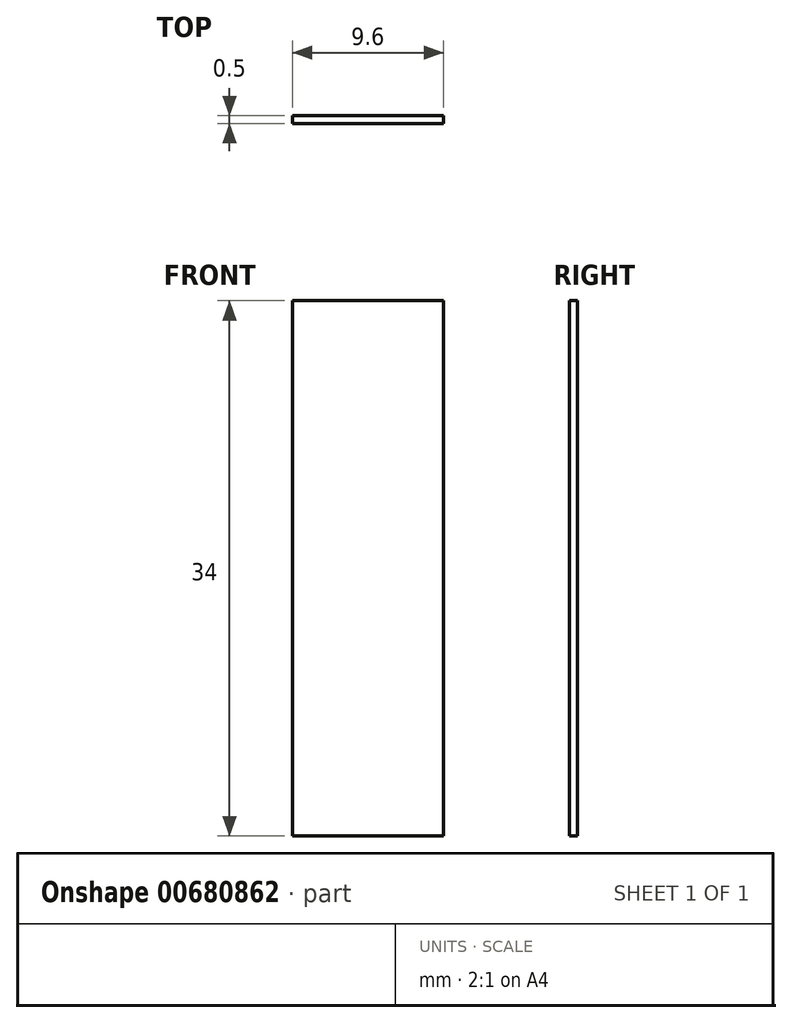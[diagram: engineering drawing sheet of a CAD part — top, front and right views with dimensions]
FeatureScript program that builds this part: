
annotation { "Feature Type Name" : "Feature", "Feature Type Description" : "" }
export const myFeature = defineFeature(function(context is Context, id is Id, definition is map)
    precondition{}
    {
        {
            var Q0;
            Q0=qCreatedBy(makeId("Front.planeOp"),FACE);
            var sketch = newSketch(context, id + "F0", { "sketchPlane" : qUnion([Q0])});
            skLineSegment(sketch, "E0.bottom", {"start": v(-4.8, 17) * mm, "end": v(4.8, 17) * mm});
            skLineSegment(sketch, "E0.top", {"start": v(-4.8, -17) * mm, "end": v(4.8, -17) * mm});
            skLineSegment(sketch, "E0.left", {"start": v(-4.8, 17) * mm, "end": v(-4.8, -17) * mm});
            skLineSegment(sketch, "E0.right", {"start": v(4.8, 17) * mm, "end": v(4.8, -17) * mm});
            skSolve(sketch);
        }
        {
            var Q0;
            Q0=makeQuery(id+"F0.imprint","IMPRINT",FACE,{"disambiguationData":[TD([[makeQuery(id+"F0.imprint","IMPRINT",EDGE,{"derivedFrom":sQuery(id+"F0.wireOp",EDGE,"E0.bottom")}),-1.0]])]});
            extrude(context, id + "F1", {"entities" : qUnion([Q0]), "depth" : 0.5 * mm, "offsetDistance" : 25.4 * mm});
        }
    });
